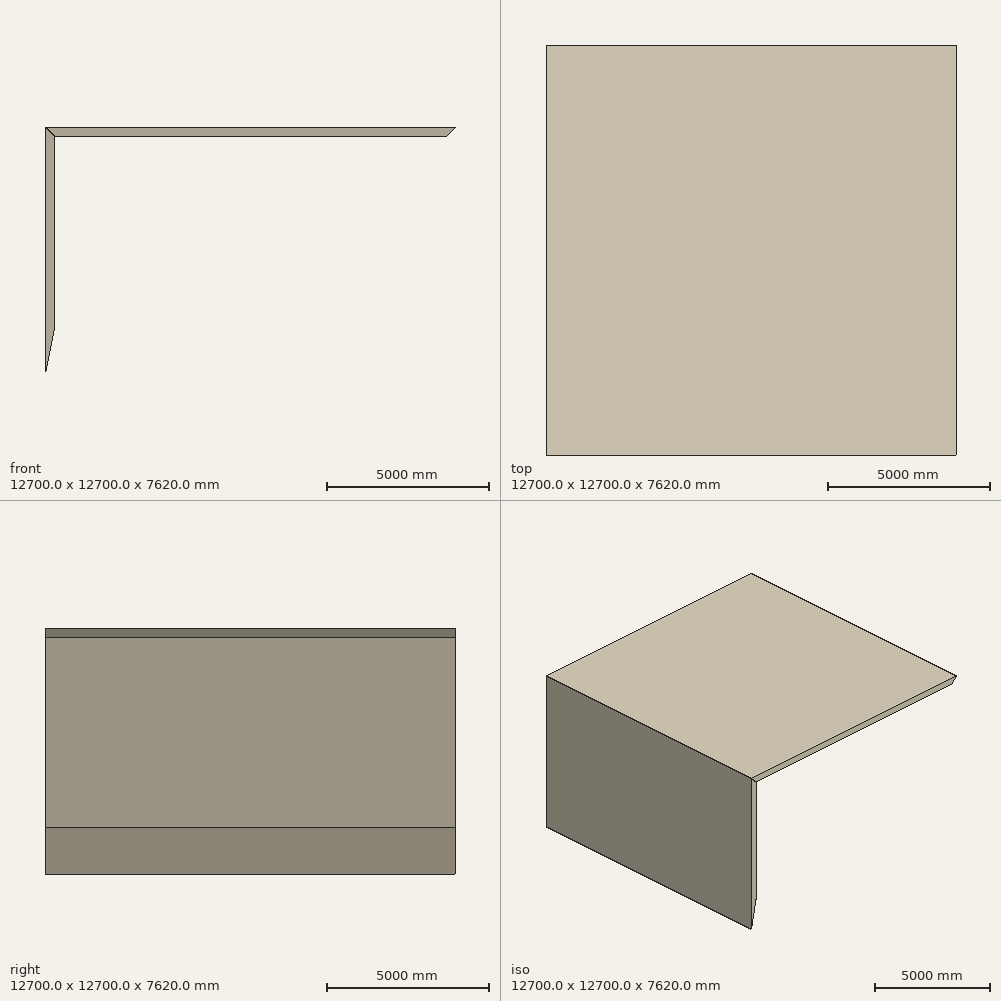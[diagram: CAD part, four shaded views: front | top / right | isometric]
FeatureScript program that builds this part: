
annotation { "Feature Type Name" : "Feature", "Feature Type Description" : "" }
export const myFeature = defineFeature(function(context is Context, id is Id, definition is map)
    precondition{}
    {
        {
            var Q0;
            Q0=qCreatedBy(makeId("Front.planeOp"),FACE);
            var sketch = newSketch(context, id + "F0", { "sketchPlane" : qUnion([Q0])});
            skLineSegment(sketch, "E0.bottom", {"start": v(6350, 3810) * mm, "end": v(-6350, 3810) * mm});
            skLineSegment(sketch, "E0.top", {"start": v(6350, -3810) * mm, "end": v(-6350, -3810) * mm});
            skLineSegment(sketch, "E0.left", {"start": v(6350, 3810) * mm, "end": v(6350, -3810) * mm});
            skLineSegment(sketch, "E0.right", {"start": v(-6350, 3810) * mm, "end": v(-6350, -3810) * mm});
            skPoint(sketch, "E0.middle", {"position": v(0, 0) * mm});
            skLineSegment(sketch, "E1.bottom", {"start": v(-6056.6, 3526.22) * mm, "end": v(6096, 3526.22) * mm});
            skLineSegment(sketch, "E1.top", {"start": v(-6056.6, -2365.02) * mm, "end": v(6096, -2365.02) * mm});
            skLineSegment(sketch, "E1.left", {"start": v(-6056.6, 3526.22) * mm, "end": v(-6056.6, -2365.02) * mm});
            skLineSegment(sketch, "E1.right", {"start": v(6096, 3526.22) * mm, "end": v(6096, -2365.02) * mm});
            skLineSegment(sketch, "E2", {"start": v(1122.87, -3553.03) * mm, "end": v(1122.87, 447.93) * mm});
            skLineSegment(sketch, "E3", {"start": v(6350, 3810) * mm, "end": v(6096, 3526.22) * mm});
            skLineSegment(sketch, "E4", {"start": v(-6056.6, -2365.02) * mm, "end": v(-6350, -3810) * mm});
            skLineSegment(sketch, "E5", {"start": v(-6056.6, 3526.22) * mm, "end": v(-6350, 3810) * mm});
            skSolve(sketch);
        }
        {
            var Q0;
            Q0=makeQuery(id+"F0.imprint","IMPRINT",FACE,{"disambiguationData":[TD([[makeQuery(id+"F0.imprint","IMPRINT",EDGE,{"derivedFrom":sQuery(id+"F0.wireOp",EDGE,"E0.bottom")}),1.0]])]});
            var sketch = newSketch(context, id + "F1", { "sketchPlane" : qUnion([Q0])});
            skSolve(sketch);
        }
        {
            var Q0;
            Q0=makeQuery(id+"F0.imprint","IMPRINT",FACE,{"disambiguationData":[TD([[makeQuery(id+"F0.imprint","IMPRINT",EDGE,{"derivedFrom":sQuery(id+"F0.wireOp",EDGE,"E0.right")}),1.0]])]});
            extrude(context, id + "F2", {"entities" : qUnion([Q0]), "depth" : 12700 * mm});
        }
        {
            var Q0;
            Q0=makeQuery(id+"F2.opExtrude","CAP_EDGE",EDGE,{"disambiguationData":[OSD([sQuery(id+"F0.wireOp",EDGE,"E0.right")])],"isStart":false});
            fillet(context, id + "F3", {"entities" : qUnion([Q0]), "radius" : 12.7 * mm, "tangentPropagation" : true, "allowEdgeOverflow" : false});
        }
        {
            var Q0;
            Q0=makeQuery(id+"F1.imprint","IMPRINT",FACE,{"disambiguationData":[TD([[makeQuery(id+"F1.imprint","IMPRINT",EDGE,{"derivedFrom":makeQuery(id+"F0.imprint","IMPRINT",EDGE,{"derivedFrom":sQuery(id+"F0.wireOp",EDGE,"E0.bottom")})}),1.0]])]});
            var Q1;
            Q1=makeQuery(id+"F2.opExtrude","CAP_FACE",FACE,{"disambiguationData":[OSD([sQuery(id+"F0.wireOp",EDGE,"E0.right"),sQuery(id+"F0.wireOp",EDGE,"E1.left"),sQuery(id+"F0.wireOp",EDGE,"E4"),sQuery(id+"F0.wireOp",EDGE,"E5")])],"isStart":false});
            extrude(context, id + "F4", {"entities" : qUnion([Q0]), "endBound" : BoundingType.UP_TO_SURFACE, "endBoundEntityFace" : qUnion([Q1]), "depth" : 8966.2 * mm});
        }
    });
